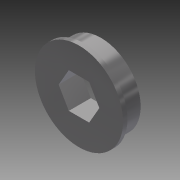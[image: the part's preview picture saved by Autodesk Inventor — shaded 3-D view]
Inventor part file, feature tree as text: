
AUTODESK INVENTOR PART (.ipt)
format: ipt  version: 2014 (Build 180170000, 170)  size: 117,760 bytes
history: native  units: in
note: dims shown in document units (in); Inventor stores cm internally (conversion verified against a paired STEP export)
features: extrude x2, sketch x2
ambient origin geometry x8: Origin, YZ Plane, XZ Plane, XY Plane, X Axis, Y Axis, Z Axis, Center Point
bodies: Solid1 (feature_tree)
feature tree (4):
  extrude  "Extrusion1"  Depth=0.5in
  extrude  "Extrusion2"  Depth=0.0625in
  sketch  "Sketch1"  dims[d0=0.5in d1=1.125in]
  sketch  "Sketch2"  dims[d2=0.25in d3=0.0in d4=0.0625in d5=0.0625in d6=0.0in]
